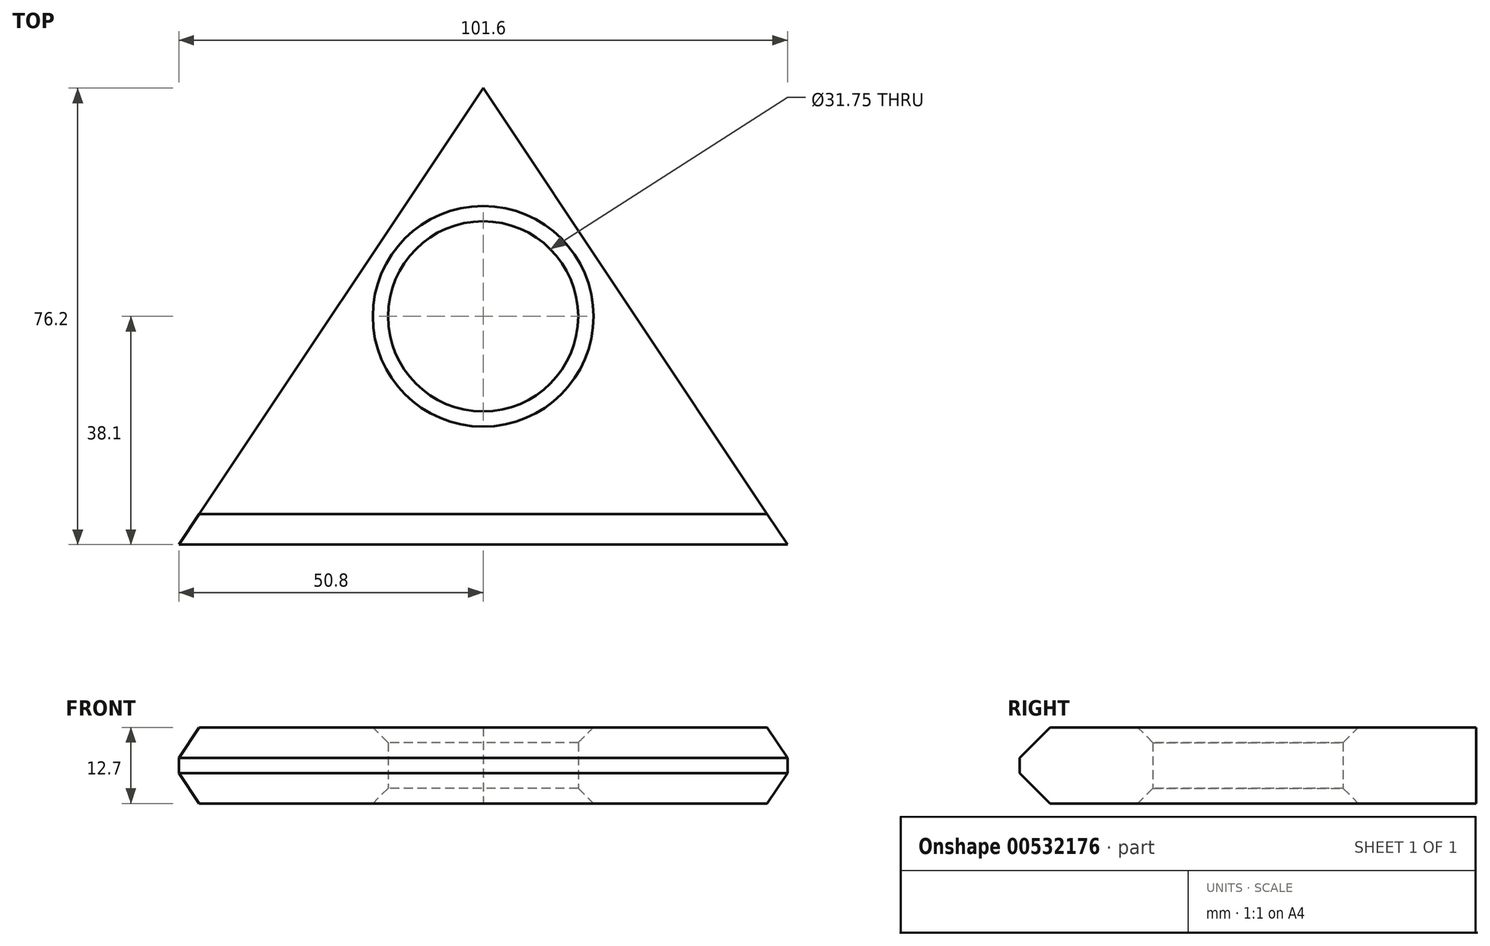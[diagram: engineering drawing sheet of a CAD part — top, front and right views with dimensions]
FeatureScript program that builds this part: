
annotation { "Feature Type Name" : "Feature", "Feature Type Description" : "" }
export const myFeature = defineFeature(function(context is Context, id is Id, definition is map)
    precondition{}
    {
        {
            var Q0;
            Q0=qCreatedBy(makeId("Top.planeOp"),FACE);
            var sketch = newSketch(context, id + "F0", { "sketchPlane" : qUnion([Q0])});
            skLineSegment(sketch, "E0", {"start": v(-50.8, 0) * mm, "end": v(0, 76.2) * mm});
            skLineSegment(sketch, "E1", {"start": v(0, 76.2) * mm, "end": v(50.8, 0) * mm});
            skLineSegment(sketch, "E2", {"start": v(50.8, 0) * mm, "end": v(-50.8, 0) * mm});
            skCircle(sketch, "E3", {"center": v(0, 38.1) * mm, "radius": 15.88 * mm});
            skSolve(sketch);
        }
        {
            var Q0;
            Q0=makeQuery(id+"F0.imprint","IMPRINT",FACE,{"disambiguationData":[TD([[makeQuery(id+"F0.imprint","IMPRINT",EDGE,{"derivedFrom":sQuery(id+"F0.wireOp",EDGE,"E0")}),-1.0]])]});
            extrude(context, id + "F1", {"entities" : qUnion([Q0]), "depth" : 12.7 * mm, "offsetDistance" : 25.4 * mm});
        }
        {
            var Q0;
            Q0=makeQuery(id+"F1.opExtrude","CAP_EDGE",EDGE,{"disambiguationData":[OSD([sQuery(id+"F0.wireOp",EDGE,"E2")])],"isStart":false});
            var Q1;
            Q1=makeQuery(id+"F1.opExtrude","CAP_EDGE",EDGE,{"disambiguationData":[OSD([sQuery(id+"F0.wireOp",EDGE,"E2")])],"isStart":true});
            chamfer(context, id + "F2", {"entities" : qUnion([Q0, Q1]), "width" : 5.08 * mm, "tangentPropagation" : true});
        }
        {
            var Q0;
            Q0=makeQuery(id+"F1.opExtrude","CAP_EDGE",EDGE,{"disambiguationData":[OSD([sQuery(id+"F0.wireOp",EDGE,"E3")])],"isStart":true});
            var Q1;
            Q1=makeQuery(id+"F1.opExtrude","CAP_EDGE",EDGE,{"disambiguationData":[OSD([sQuery(id+"F0.wireOp",EDGE,"E3")])],"isStart":false});
            chamfer(context, id + "F3", {"entities" : qUnion([Q0, Q1]), "width" : 2.54 * mm, "tangentPropagation" : true});
        }
    });
